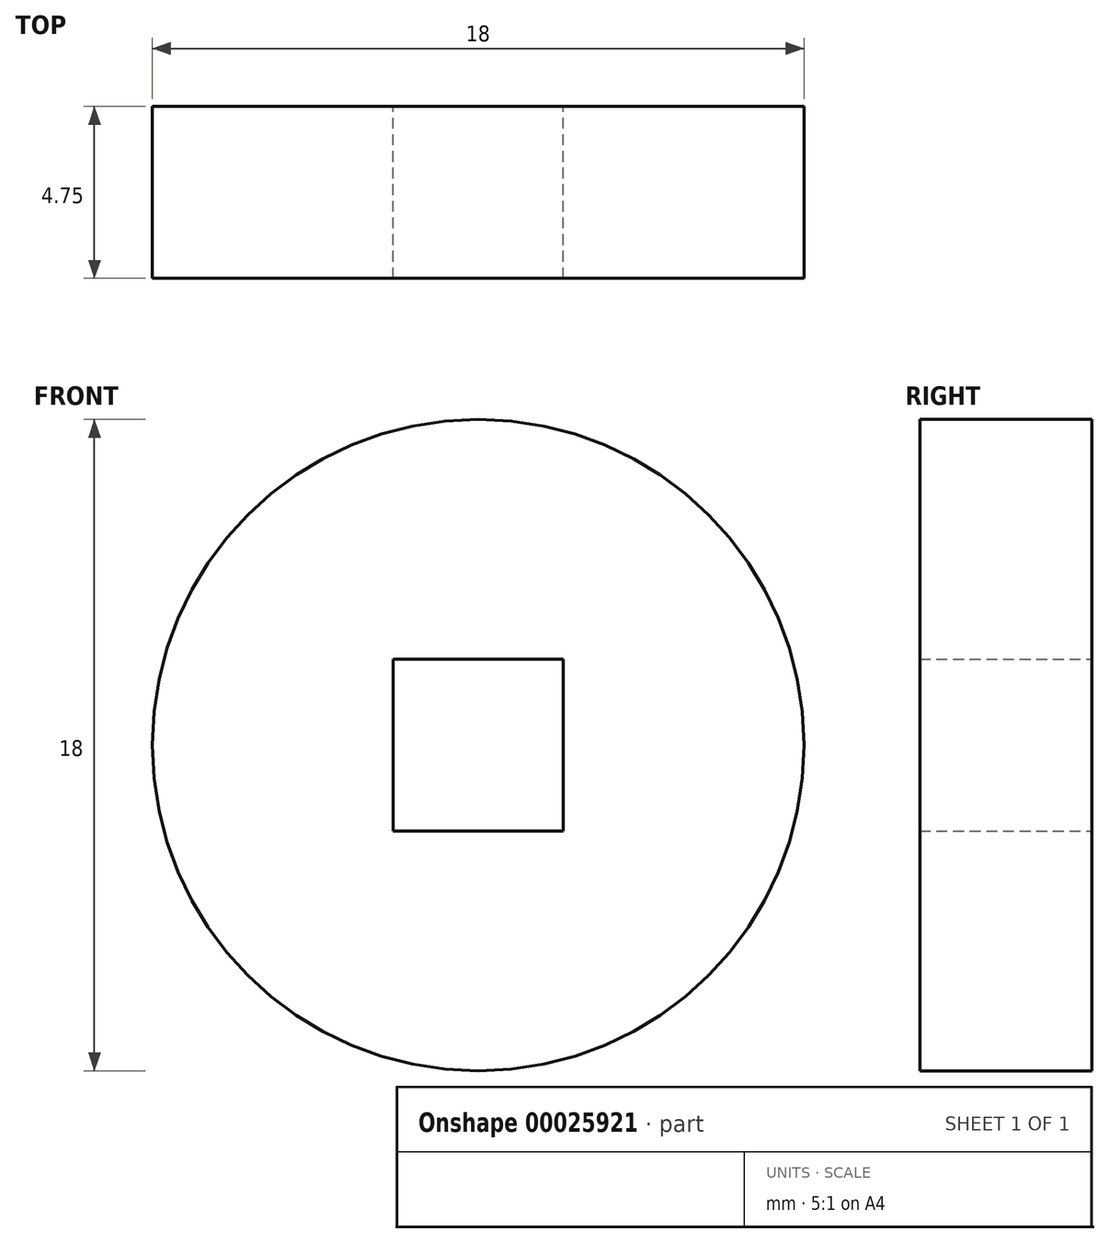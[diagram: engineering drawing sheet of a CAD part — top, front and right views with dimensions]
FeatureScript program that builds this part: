
annotation { "Feature Type Name" : "Feature", "Feature Type Description" : "" }
export const myFeature = defineFeature(function(context is Context, id is Id, definition is map)
    precondition{}
    {
        {
            var Q0;
            Q0=qCreatedBy(makeId("Front.planeOp"),FACE);
            var sketch = newSketch(context, id + "F0", { "sketchPlane" : qUnion([Q0])});
            skCircle(sketch, "E0", {"center": v(0, 0) * mm, "radius": 9 * mm});
            skLineSegment(sketch, "E1.rect.bottom", {"start": v(2.35, 2.38) * mm, "end": v(-2.35, 2.38) * mm});
            skLineSegment(sketch, "E1.rect.top", {"start": v(2.35, -2.38) * mm, "end": v(-2.35, -2.38) * mm});
            skLineSegment(sketch, "E1.rect.left", {"start": v(2.35, 2.38) * mm, "end": v(2.35, -2.38) * mm});
            skLineSegment(sketch, "E1.rect.right", {"start": v(-2.35, 2.38) * mm, "end": v(-2.35, -2.38) * mm});
            skSolve(sketch);
        }
        {
            var Q0;
            Q0=makeQuery(id+"F0.imprint","IMPRINT",FACE,{"disambiguationData":[TD([[makeQuery(id+"F0.imprint","IMPRINT",EDGE,{"derivedFrom":sQuery(id+"F0.wireOp",EDGE,"5f4a554a-107a-4ad8-bc78-8fd444699d9d")}),-1.0]])]});
            var Q1;
            Q1=makeQuery(id+"F0.imprint","IMPRINT",FACE,{"disambiguationData":[TD([[makeQuery(id+"F0.imprint","IMPRINT",EDGE,{"derivedFrom":sQuery(id+"F0.wireOp",EDGE,"E0")}),1.0]])]});
            extrude(context, id + "F1", {"entities" : qUnion([Q0, Q1]), "depth" : 4.75 * mm});
        }
    });
